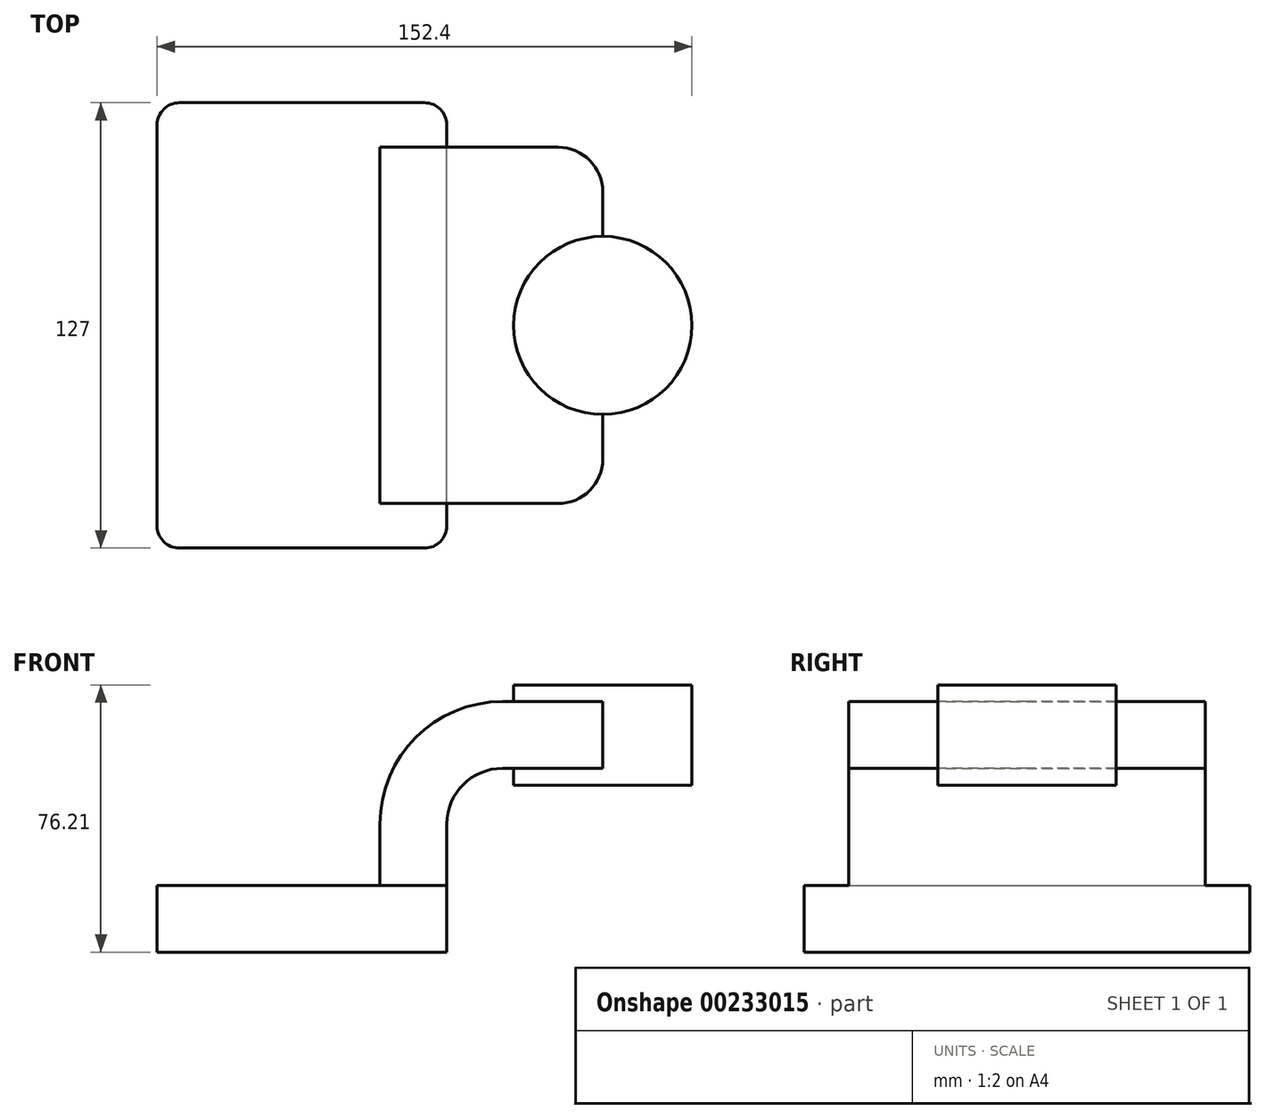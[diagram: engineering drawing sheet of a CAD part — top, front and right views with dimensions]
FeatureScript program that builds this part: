
annotation { "Feature Type Name" : "Feature", "Feature Type Description" : "" }
export const myFeature = defineFeature(function(context is Context, id is Id, definition is map)
    precondition{}
    {
        {
            var Q0;
            Q0=qCreatedBy(makeId("Front.planeOp"),FACE);
            var sketch = newSketch(context, id + "F0", { "sketchPlane" : qUnion([Q0])});
            skLineSegment(sketch, "E0.bottom", {"start": v(-41.28, 9.52) * mm, "end": v(41.28, 9.53) * mm});
            skLineSegment(sketch, "E0.top", {"start": v(-41.27, -9.52) * mm, "end": v(41.28, -9.52) * mm});
            skLineSegment(sketch, "E0.left", {"start": v(-41.28, 9.52) * mm, "end": v(-41.28, -9.53) * mm});
            skLineSegment(sketch, "E0.right", {"start": v(41.27, 9.53) * mm, "end": v(41.28, -9.52) * mm});
            skPoint(sketch, "E0.middle", {"position": v(0, 0) * mm});
            skLineSegment(sketch, "E1.bottom", {"start": v(111.12, 38.1) * mm, "end": v(60.32, 38.1) * mm});
            skLineSegment(sketch, "E1.top", {"start": v(111.12, 66.68) * mm, "end": v(60.32, 66.68) * mm});
            skLineSegment(sketch, "E1.left", {"start": v(111.12, 38.1) * mm, "end": v(111.12, 66.68) * mm});
            skLineSegment(sketch, "E1.right", {"start": v(60.32, 38.1) * mm, "end": v(60.32, 66.68) * mm});
            skPoint(sketch, "E1.middle", {"position": v(85.72, 52.39) * mm});
            skLineSegment(sketch, "E2", {"start": v(41.27, 9.53) * mm, "end": v(41.27, 27) * mm});
            skArc(sketch, "E3", {"start": v(41.27, 27) * mm, "mid": v(45.92, 38.23) * mm, "end": v(57.15, 42.88) * mm});
            skLineSegment(sketch, "E4", {"start": v(57.15, 42.88) * mm, "end": v(85.72, 42.88) * mm});
            skLineSegment(sketch, "E5.0", {"start": v(57.15, 61.93) * mm, "end": v(85.72, 61.93) * mm});
            skArc(sketch, "E5.1", {"start": v(22.22, 27) * mm, "mid": v(32.45, 51.7) * mm, "end": v(57.15, 61.93) * mm});
            skLineSegment(sketch, "E5.2", {"start": v(22.22, 9.52) * mm, "end": v(22.22, 27) * mm});
            skLineSegment(sketch, "E6", {"start": v(85.72, 38.1) * mm, "end": v(85.72, 66.68) * mm});
            skFitSpline(sketch, "E7", {"points": [v(-41.27, 9.52) * mm, v(57.15, 61.93) * mm], "startDerivative": vector(0, 87.82) * mm, "endDerivative": vector(136.39, 0) * mm});
            skSolve(sketch);
        }
        {
            var Q0;
            Q0=makeQuery(id+"F0.imprint","IMPRINT",FACE,{"disambiguationData":[TD([[makeQuery(id+"F0.imprint","IMPRINT",EDGE,{"derivedFrom":sQuery(id+"F0.wireOp",EDGE,"E0.top")}),1.0]])]});
            extrude(context, id + "F1", {"entities" : qUnion([Q0]), "endBound" : BoundingType.SYMMETRIC, "depth" : 127 * mm});
        }
        {
            var Q0;
            {var subQ1=sQuery(id+"F0.wireOp",EDGE,"E2");Q0=makeQuery(id+"F0.imprint","IMPRINT",FACE,{"disambiguationData":[TD([[makeQuery(id+"F0.imprint","IMPRINT",EDGE,{"derivedFrom":subQ1}),1.0]])]});}
            var Q1;
            {var subQ0=sQuery(id+"F0.wireOp",EDGE,"E4");var subQ1=sQuery(id+"F0.wireOp",EDGE,"E1.right");var subQ2=makeQuery(id+"F0.imprint","INTERSECT",VERTEX,{"derivedFrom":[subQ1,subQ0]});Q1=makeQuery(id+"F0.imprint","IMPRINT",FACE,{"disambiguationData":[TD([[makeQuery(id+"F0.imprint","IMPRINT",EDGE,{"disambiguationData":[TD([[subQ2,-1.0]])],"derivedFrom":subQ1}),-1.0]])]});}
            extrude(context, id + "F2", {"entities" : qUnion([Q0, Q1]), "operationType" : NewBodyOperationType.ADD, "endBound" : BoundingType.SYMMETRIC, "depth" : 101.6 * mm});
        }
        {
            var Q0;
            Q0=makeQuery(id+"F0.imprint","IMPRINT",FACE,{"disambiguationData":[TD([[makeQuery(id+"F0.imprint","IMPRINT",EDGE,{"derivedFrom":sQuery(id+"F0.wireOp",EDGE,"E5.1")}),1.0]])]});
            extrude(context, id + "F3", {"entities" : qUnion([Q0]), "operationType" : NewBodyOperationType.ADD, "endBound" : BoundingType.SYMMETRIC, "depth" : 76.2 * mm});
        }
        {
            var Q0;
            {var subQ0=sQuery(id+"F0.wireOp",EDGE,"E1.left");Q0=makeQuery(id+"F0.imprint","IMPRINT",FACE,{"disambiguationData":[TD([[makeQuery(id+"F0.imprint","IMPRINT",EDGE,{"derivedFrom":subQ0}),1.0]])]});}
            var Q1;
            Q1=sQuery(id+"F0.wireOp",EDGE,"E6");
            revolve(context, id + "F4", {"operationType" : NewBodyOperationType.ADD, "entities" : qUnion([Q0]), "axis" : qUnion([Q1]), "revolveType" : RevolveType.FULL});
        }
        {
            var Q0;
            Q0=makeQuery(id+"F1.opExtrude","CAP_EDGE",EDGE,{"disambiguationData":[OSD([sQuery(id+"F0.wireOp",EDGE,"E0.right")])],"isStart":false});
            var Q1;
            Q1=makeQuery(id+"F1.opExtrude","CAP_EDGE",EDGE,{"disambiguationData":[OSD([sQuery(id+"F0.wireOp",EDGE,"E0.right")])],"isStart":true});
            var Q2;
            Q2=makeQuery(id+"F1.opExtrude","CAP_EDGE",EDGE,{"disambiguationData":[OSD([sQuery(id+"F0.wireOp",EDGE,"E0.left")])],"isStart":true});
            var Q3;
            Q3=makeQuery(id+"F1.opExtrude","CAP_EDGE",EDGE,{"disambiguationData":[OSD([sQuery(id+"F0.wireOp",EDGE,"E0.left")])],"isStart":false});
            fillet(context, id + "F5", {"entities" : qUnion([Q0, Q1, Q2, Q3]), "radius" : 6.35 * mm, "tangentPropagation" : true, "allowEdgeOverflow" : false});
        }
        {
            var Q0;
            Q0=makeQuery(id+"F2.opExtrude","CAP_EDGE",EDGE,{"disambiguationData":[OSD([sQuery(id+"F0.wireOp",EDGE,"E6")])],"isStart":false});
            var Q1;
            Q1=makeQuery(id+"F2.opExtrude","CAP_EDGE",EDGE,{"disambiguationData":[OSD([sQuery(id+"F0.wireOp",EDGE,"E6")])],"isStart":true});
            fillet(context, id + "F6", {"entities" : qUnion([Q0, Q1]), "radius" : 12.7 * mm, "tangentPropagation" : true, "allowEdgeOverflow" : false});
        }
    });
